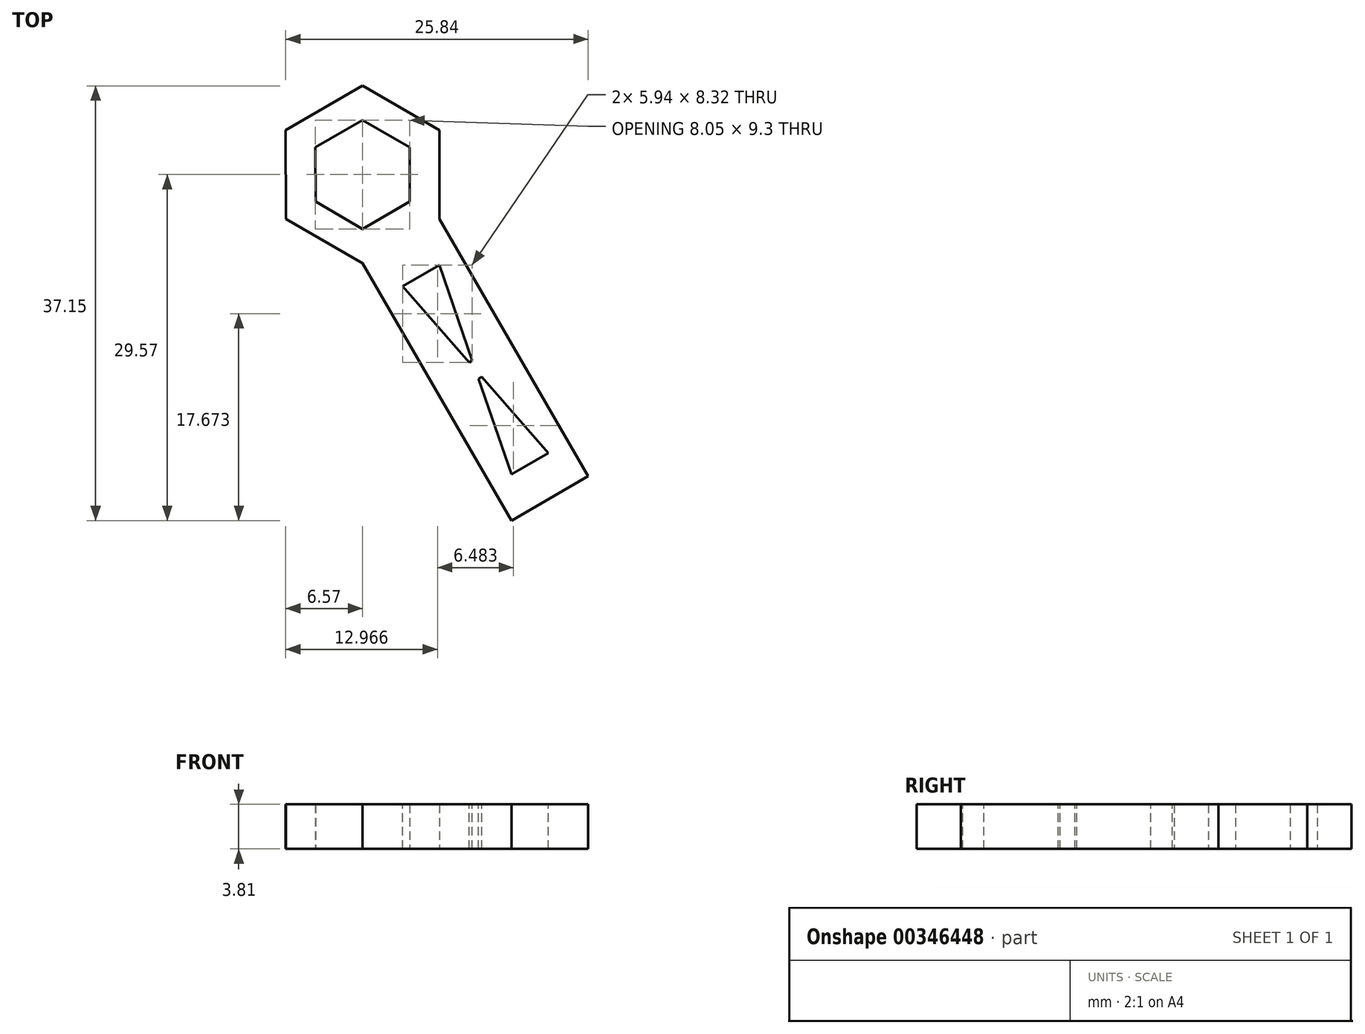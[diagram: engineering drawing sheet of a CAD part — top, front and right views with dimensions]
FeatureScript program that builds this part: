
annotation { "Feature Type Name" : "Feature", "Feature Type Description" : "" }
export const myFeature = defineFeature(function(context is Context, id is Id, definition is map)
    precondition{}
    {
        {
            var Q0;
            Q0=qCreatedBy(makeId("Top.planeOp"),FACE);
            var sketch = newSketch(context, id + "F0", { "sketchPlane" : qUnion([Q0])});
            skCircle(sketch, "E0.cCircle", {"center": v(0, 0) * mm, "radius": 4.03 * mm, "construction": true});
            skLineSegment(sketch, "E0.0", {"start": v(0, 4.65) * mm, "end": v(4.02, 2.33) * mm});
            skLineSegment(sketch, "E0.1", {"start": v(4.02, 2.33) * mm, "end": v(4.03, -2.32) * mm});
            skLineSegment(sketch, "E0.2", {"start": v(4.03, -2.32) * mm, "end": v(0, -4.65) * mm});
            skLineSegment(sketch, "E0.3", {"start": v(0, -4.65) * mm, "end": v(-4.02, -2.33) * mm});
            skLineSegment(sketch, "E0.4", {"start": v(-4.02, -2.33) * mm, "end": v(-4.03, 2.32) * mm});
            skLineSegment(sketch, "E0.5", {"start": v(-4.03, 2.32) * mm, "end": v(0, 4.65) * mm});
            skPoint(sketch, "E0.0.midPoint", {"position": v(2.01, 3.49) * mm});
            skCircle(sketch, "E1.cCircle", {"center": v(0, 0) * mm, "radius": 6.57 * mm, "construction": true});
            skLineSegment(sketch, "E1.0", {"start": v(0, 7.58) * mm, "end": v(6.56, 3.8) * mm});
            skLineSegment(sketch, "E1.1", {"start": v(6.56, 3.8) * mm, "end": v(6.57, -3.79) * mm});
            skLineSegment(sketch, "E1.2", {"start": v(6.57, -3.79) * mm, "end": v(0, -7.58) * mm});
            skLineSegment(sketch, "E1.3", {"start": v(0, -7.58) * mm, "end": v(-6.56, -3.8) * mm});
            skLineSegment(sketch, "E1.4", {"start": v(-6.56, -3.8) * mm, "end": v(-6.57, 3.79) * mm});
            skLineSegment(sketch, "E1.5", {"start": v(-6.57, 3.79) * mm, "end": v(0, 7.58) * mm});
            skPoint(sketch, "E1.0.midPoint", {"position": v(3.28, 5.69) * mm});
            skSolve(sketch);
        }
        {
            var Q0;
            Q0=qSketchRegion(id+"F0",true);
            extrude(context, id + "F1", {"entities" : qUnion([Q0]), "depth" : 3.8 * mm});
        }
        {
            var Q0;
            Q0=makeQuery(id+"F1.opExtrude","SWEPT_FACE",FACE,{"disambiguationData":[OSD([sQuery(id+"F0.wireOp",EDGE,"E1.2")])]});
            extrude(context, id + "F2", {"entities" : qUnion([Q0]), "operationType" : NewBodyOperationType.ADD, "depth" : 25.4 * mm});
        }
        {
            var Q0;
            {var subQ0=sQuery(id+"F0.wireOp",EDGE,"E1.2");Q0=makeQuery(id+"F2.boolean.opBoolean","MERGE",FACE,{"derivedFrom":[makeQuery(id+"F1.opExtrude","CAP_FACE",FACE,{"disambiguationData":[OSD([sQuery(id+"F0.wireOp",EDGE,"E0.0"),sQuery(id+"F0.wireOp",EDGE,"E0.1"),sQuery(id+"F0.wireOp",EDGE,"E0.2"),sQuery(id+"F0.wireOp",EDGE,"E0.3"),sQuery(id+"F0.wireOp",EDGE,"E0.4"),sQuery(id+"F0.wireOp",EDGE,"E0.5"),sQuery(id+"F0.wireOp",EDGE,"E1.0"),sQuery(id+"F0.wireOp",EDGE,"E1.1"),subQ0,sQuery(id+"F0.wireOp",EDGE,"E1.3"),sQuery(id+"F0.wireOp",EDGE,"E1.4"),sQuery(id+"F0.wireOp",EDGE,"E1.5")])],"isStart":false}),makeQuery(id+"F2.opExtrude","SWEPT_FACE",FACE,{"disambiguationData":[OSD([subQ0]),TDD([makeQuery(id+"F1.opExtrude","CAP_EDGE",EDGE,{"disambiguationData":[OSD([subQ0])],"isStart":false})])]})]});}
            var sketch = newSketch(context, id + "F3", { "sketchPlane" : qUnion([Q0])});
            skLineSegment(sketch, "E2", {"start": v(6.36, -18.58) * mm, "end": v(12.92, -14.78) * mm});
            skLineSegment(sketch, "E3", {"start": v(9.64, -16.68) * mm, "end": v(14.28, -24.72) * mm});
            skLineSegment(sketch, "E4", {"start": v(14.28, -24.72) * mm, "end": v(12.7, -25.62) * mm});
            skLineSegment(sketch, "E5", {"start": v(12.7, -25.62) * mm, "end": v(8.07, -17.59) * mm});
            skPoint(sketch, "E6.endSnap0", {"position": v(16, -27.68) * mm});
            skLineSegment(sketch, "E7", {"start": v(14.28, -24.72) * mm, "end": v(15.85, -23.8) * mm});
            skLineSegment(sketch, "E8", {"start": v(15.85, -23.8) * mm, "end": v(9.64, -16.68) * mm});
            skLineSegment(sketch, "E9", {"start": v(12.7, -25.62) * mm, "end": v(9.64, -16.68) * mm});
            skLineSegment(sketch, "E10.MirrorCS", {"start": v(3.42, -9.55) * mm, "end": v(9.64, -16.68) * mm});
            skLineSegment(sketch, "E11.MirrorCS", {"start": v(6.57, -7.74) * mm, "end": v(9.64, -16.68) * mm});
            skLineSegment(sketch, "E12.MirrorCS", {"start": v(5, -8.65) * mm, "end": v(6.57, -7.74) * mm});
            skLineSegment(sketch, "E13.MirrorCS", {"start": v(5, -8.65) * mm, "end": v(3.42, -9.55) * mm});
            skLineSegment(sketch, "E14", {"start": v(9.9, -17.47) * mm, "end": v(9.1, -16.06) * mm});
            skLineSegment(sketch, "E15", {"start": v(9.1, -16.06) * mm, "end": v(9.37, -15.9) * mm});
            skLineSegment(sketch, "E16", {"start": v(9.37, -15.9) * mm, "end": v(10.18, -17.3) * mm});
            skLineSegment(sketch, "E17", {"start": v(9.9, -17.47) * mm, "end": v(10.18, -17.3) * mm});
            skSolve(sketch);
        }
        {
            var Q0;
            {var subQ0=sQuery(id+"F3.wireOp",EDGE,"E12.MirrorCS");Q0=makeQuery(id+"F3.imprint","IMPRINT",FACE,{"disambiguationData":[TD([[makeQuery(id+"F3.imprint","IMPRINT",EDGE,{"derivedFrom":subQ0}),-1.0]])]});}
            var Q1;
            {var subQ0=sQuery(id+"F3.wireOp",EDGE,"E4");Q1=makeQuery(id+"F3.imprint","IMPRINT",FACE,{"disambiguationData":[TD([[makeQuery(id+"F3.imprint","IMPRINT",EDGE,{"derivedFrom":subQ0}),-1.0]])]});}
            var Q2;
            {var subQ0=sQuery(id+"F3.wireOp",EDGE,"E7");Q2=makeQuery(id+"F3.imprint","IMPRINT",FACE,{"disambiguationData":[TD([[makeQuery(id+"F3.imprint","IMPRINT",EDGE,{"derivedFrom":subQ0}),1.0]])]});}
            extrude(context, id + "F4", {"entities" : qUnion([Q0, Q1, Q2]), "operationType" : NewBodyOperationType.REMOVE, "oppositeDirection" : true, "depth" : 25.4 * mm});
        }
    });
